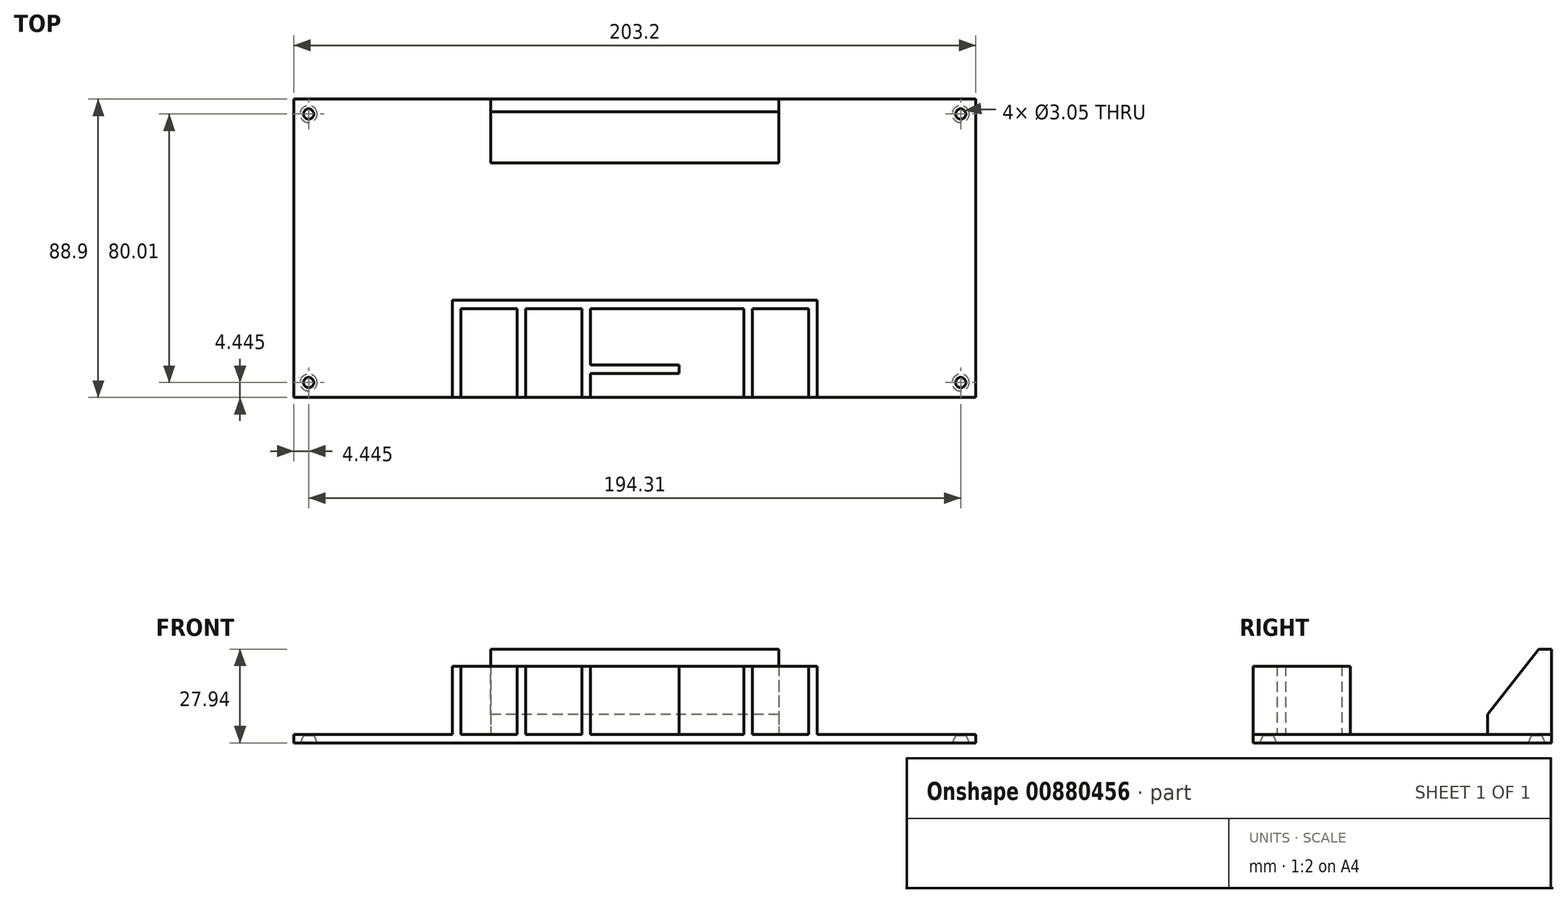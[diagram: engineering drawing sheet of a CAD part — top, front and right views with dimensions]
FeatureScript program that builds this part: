
annotation { "Feature Type Name" : "Feature", "Feature Type Description" : "" }
export const myFeature = defineFeature(function(context is Context, id is Id, definition is map)
    precondition{}
    {
        {
            var Q0;
            Q0=qCreatedBy(makeId("Top.planeOp"),FACE);
            var sketch = newSketch(context, id + "F0", { "sketchPlane" : qUnion([Q0])});
            skLineSegment(sketch, "E0.bottom", {"start": v(101.6, -44.45) * mm, "end": v(-101.6, -44.45) * mm});
            skLineSegment(sketch, "E0.top", {"start": v(101.6, 44.45) * mm, "end": v(-101.6, 44.45) * mm});
            skLineSegment(sketch, "E0.left", {"start": v(101.6, -44.45) * mm, "end": v(101.6, 44.45) * mm});
            skLineSegment(sketch, "E0.right", {"start": v(-101.6, -44.45) * mm, "end": v(-101.6, 44.45) * mm});
            skPoint(sketch, "E0.middle", {"position": v(0, 0) * mm});
            skSolve(sketch);
        }
        {
            var Q0;
            Q0 = qSketchRegion(id + "F0", true);
            extrude(context, id + "F1", {"entities" : qUnion([Q0]), "depth" : 2.54 * mm, "offsetDistance" : 25.4 * mm});
        }
        {
            var Q0;
            Q0=makeQuery(id+"F1.opExtrude","CAP_FACE",FACE,{"disambiguationData":[OSD([sQuery(id+"F0.wireOp",EDGE,"E0.bottom"),sQuery(id+"F0.wireOp",EDGE,"E0.top"),sQuery(id+"F0.wireOp",EDGE,"E0.left"),sQuery(id+"F0.wireOp",EDGE,"E0.right")])],"isStart":false});
            var sketch = newSketch(context, id + "F2", { "sketchPlane" : qUnion([Q0])});
            skLineSegment(sketch, "E1.bottom", {"start": v(-15.75, -44.45) * mm, "end": v(15.75, -44.45) * mm});
            skLineSegment(sketch, "E1.left", {"start": v(-15.75, -44.45) * mm, "end": v(-15.75, -15.5) * mm});
            skLineSegment(sketch, "E1.right", {"start": v(15.75, -44.45) * mm, "end": v(15.75, -15.5) * mm});
            skLineSegment(sketch, "E2.bottom", {"start": v(-32.51, -44.45) * mm, "end": v(-35.05, -44.45) * mm});
            skLineSegment(sketch, "E2.left", {"start": v(-32.51, -44.45) * mm, "end": v(-32.51, -15.5) * mm});
            skLineSegment(sketch, "E2.right", {"start": v(-35.05, -44.45) * mm, "end": v(-35.05, -15.5) * mm});
            skLineSegment(sketch, "E3.bottom", {"start": v(-54.36, -44.45) * mm, "end": v(-51.82, -44.45) * mm});
            skLineSegment(sketch, "E3.left", {"start": v(-54.36, -44.45) * mm, "end": v(-54.36, -15.5) * mm});
            skLineSegment(sketch, "E3.right", {"start": v(-51.82, -44.45) * mm, "end": v(-51.82, -15.5) * mm});
            skLineSegment(sketch, "E4.bottom", {"start": v(32.51, -44.45) * mm, "end": v(35.05, -44.45) * mm});
            skLineSegment(sketch, "E4.left", {"start": v(32.51, -44.45) * mm, "end": v(32.51, -15.5) * mm});
            skLineSegment(sketch, "E4.right", {"start": v(35.05, -44.45) * mm, "end": v(35.05, -15.5) * mm});
            skLineSegment(sketch, "E5.bottom", {"start": v(51.82, -44.45) * mm, "end": v(54.36, -44.45) * mm});
            skLineSegment(sketch, "E5.left", {"start": v(51.82, -44.45) * mm, "end": v(51.82, -15.5) * mm});
            skLineSegment(sketch, "E5.right", {"start": v(54.36, -44.45) * mm, "end": v(54.36, -15.5) * mm});
            skLineSegment(sketch, "E6", {"start": v(-54.36, -15.5) * mm, "end": v(54.36, -15.5) * mm});
            skLineSegment(sketch, "E7", {"start": v(-54.36, -18.03) * mm, "end": v(51.82, -18.03) * mm});
            skLineSegment(sketch, "E8", {"start": v(51.82, -18.03) * mm, "end": v(54.36, -18.03) * mm});
            skLineSegment(sketch, "E9", {"start": v(-13.2, -44.45) * mm, "end": v(-13.2, -15.5) * mm});
            skLineSegment(sketch, "E10", {"start": v(13.2, -44.45) * mm, "end": v(13.2, -15.5) * mm});
            skLineSegment(sketch, "E11", {"start": v(-13.2, -34.8) * mm, "end": v(13.2, -34.8) * mm});
            skLineSegment(sketch, "E12", {"start": v(13.2, -34.8) * mm, "end": v(13.2, -37.34) * mm});
            skLineSegment(sketch, "E13", {"start": v(13.2, -37.34) * mm, "end": v(-13.2, -37.34) * mm});
            skLineSegment(sketch, "E14.bottom", {"start": v(-42.91, 25.4) * mm, "end": v(42.91, 25.4) * mm});
            skLineSegment(sketch, "E14.top", {"start": v(-42.91, 63.5) * mm, "end": v(42.91, 63.5) * mm});
            skLineSegment(sketch, "E14.left", {"start": v(-42.91, 25.4) * mm, "end": v(-42.91, 63.5) * mm});
            skLineSegment(sketch, "E14.right", {"start": v(42.91, 25.4) * mm, "end": v(42.91, 63.5) * mm});
            skPoint(sketch, "E14.middle", {"position": v(0, 44.45) * mm});
            skLineSegment(sketch, "E15", {"start": v(-42.91, 44.45) * mm, "end": v(42.91, 44.45) * mm});
            skSolve(sketch);
        }
        {
            var Q0;
            {var subQ0=sQuery(id+"F2.wireOp",EDGE,"E2.bottom");Q0=makeQuery(id+"F2.imprint","IMPRINT",FACE,{"disambiguationData":[TD([[makeQuery(id+"F2.imprint","IMPRINT",EDGE,{"derivedFrom":subQ0}),-1.0]])]});}
            var Q1;
            {var subQ0=sQuery(id+"F2.wireOp",EDGE,"E3.bottom");Q1=makeQuery(id+"F2.imprint","IMPRINT",FACE,{"disambiguationData":[TD([[makeQuery(id+"F2.imprint","IMPRINT",EDGE,{"derivedFrom":subQ0}),-1.0]])]});}
            var Q2;
            {var subQ0=sQuery(id+"F2.wireOp",EDGE,"E6");var subQ1=sQuery(id+"F2.wireOp",EDGE,"E3.left");var subQ2=makeQuery(id+"F2.imprint","INTERSECT",VERTEX,{"derivedFrom":[subQ1,subQ0]});Q2=makeQuery(id+"F2.imprint","IMPRINT",FACE,{"disambiguationData":[TD([[makeQuery(id+"F2.imprint","IMPRINT",EDGE,{"disambiguationData":[TD([[subQ2,1.0]])],"derivedFrom":subQ1}),-1.0]])]});}
            var Q3;
            {var subQ0=sQuery(id+"F2.wireOp",EDGE,"E4.bottom");Q3=makeQuery(id+"F2.imprint","IMPRINT",FACE,{"disambiguationData":[TD([[makeQuery(id+"F2.imprint","IMPRINT",EDGE,{"derivedFrom":subQ0}),-1.0]])]});}
            var Q4;
            {var subQ0=sQuery(id+"F2.wireOp",EDGE,"E5.bottom");Q4=makeQuery(id+"F2.imprint","IMPRINT",FACE,{"disambiguationData":[TD([[makeQuery(id+"F2.imprint","IMPRINT",EDGE,{"derivedFrom":subQ0}),-1.0]])]});}
            var Q5;
            {var subQ3=sQuery(id+"F2.wireOp",EDGE,"E8");Q5=makeQuery(id+"F2.imprint","IMPRINT",FACE,{"disambiguationData":[TD([[makeQuery(id+"F2.imprint","IMPRINT",EDGE,{"derivedFrom":subQ3}),1.0]])]});}
            var Q6;
            {var subQ0=sQuery(id+"F2.wireOp",EDGE,"E6");var subQ1=sQuery(id+"F2.wireOp",EDGE,"E1.left");var subQ2=makeQuery(id+"F2.imprint","INTERSECT",VERTEX,{"derivedFrom":[subQ1,subQ0]});Q6=makeQuery(id+"F2.imprint","IMPRINT",FACE,{"disambiguationData":[TD([[makeQuery(id+"F2.imprint","IMPRINT",EDGE,{"disambiguationData":[TD([[subQ2,1.0]])],"derivedFrom":subQ1}),1.0]])]});}
            var Q7;
            {var subQ0=sQuery(id+"F2.wireOp",EDGE,"E6");var subQ1=sQuery(id+"F2.wireOp",EDGE,"E1.left");var subQ2=makeQuery(id+"F2.imprint","INTERSECT",VERTEX,{"derivedFrom":[subQ1,subQ0]});Q7=makeQuery(id+"F2.imprint","IMPRINT",FACE,{"disambiguationData":[TD([[makeQuery(id+"F2.imprint","IMPRINT",EDGE,{"disambiguationData":[TD([[subQ2,1.0]])],"derivedFrom":subQ1}),-1.0]])]});}
            var Q8;
            {var subQ0=sQuery(id+"F2.wireOp",EDGE,"E6");var subQ1=sQuery(id+"F2.wireOp",EDGE,"E1.right");var subQ2=makeQuery(id+"F2.imprint","INTERSECT",VERTEX,{"derivedFrom":[subQ1,subQ0]});Q8=makeQuery(id+"F2.imprint","IMPRINT",FACE,{"disambiguationData":[TD([[makeQuery(id+"F2.imprint","IMPRINT",EDGE,{"disambiguationData":[TD([[subQ2,1.0]])],"derivedFrom":subQ1}),-1.0]])]});}
            var Q9;
            {var subQ0=sQuery(id+"F2.wireOp",EDGE,"E6");var subQ1=sQuery(id+"F2.wireOp",EDGE,"E1.right");var subQ2=makeQuery(id+"F2.imprint","INTERSECT",VERTEX,{"derivedFrom":[subQ1,subQ0]});Q9=makeQuery(id+"F2.imprint","IMPRINT",FACE,{"disambiguationData":[TD([[makeQuery(id+"F2.imprint","IMPRINT",EDGE,{"disambiguationData":[TD([[subQ2,1.0]])],"derivedFrom":subQ1}),1.0]])]});}
            var Q10;
            {var subQ0=sQuery(id+"F2.wireOp",EDGE,"E6");var subQ1=sQuery(id+"F2.wireOp",EDGE,"E2.left");var subQ2=makeQuery(id+"F2.imprint","INTERSECT",VERTEX,{"derivedFrom":[subQ1,subQ0]});Q10=makeQuery(id+"F2.imprint","IMPRINT",FACE,{"disambiguationData":[TD([[makeQuery(id+"F2.imprint","IMPRINT",EDGE,{"disambiguationData":[TD([[subQ2,1.0]])],"derivedFrom":subQ1}),1.0]])]});}
            var Q11;
            {var subQ0=sQuery(id+"F2.wireOp",EDGE,"E6");var subQ1=sQuery(id+"F2.wireOp",EDGE,"E2.right");var subQ2=makeQuery(id+"F2.imprint","INTERSECT",VERTEX,{"derivedFrom":[subQ1,subQ0]});Q11=makeQuery(id+"F2.imprint","IMPRINT",FACE,{"disambiguationData":[TD([[makeQuery(id+"F2.imprint","IMPRINT",EDGE,{"disambiguationData":[TD([[subQ2,1.0]])],"derivedFrom":subQ1}),1.0]])]});}
            var Q12;
            {var subQ0=sQuery(id+"F2.wireOp",EDGE,"E6");var subQ1=sQuery(id+"F2.wireOp",EDGE,"E4.left");var subQ2=makeQuery(id+"F2.imprint","INTERSECT",VERTEX,{"derivedFrom":[subQ1,subQ0]});Q12=makeQuery(id+"F2.imprint","IMPRINT",FACE,{"disambiguationData":[TD([[makeQuery(id+"F2.imprint","IMPRINT",EDGE,{"disambiguationData":[TD([[subQ2,1.0]])],"derivedFrom":subQ1}),-1.0]])]});}
            var Q13;
            {var subQ0=sQuery(id+"F2.wireOp",EDGE,"E6");var subQ1=sQuery(id+"F2.wireOp",EDGE,"E4.right");var subQ2=makeQuery(id+"F2.imprint","INTERSECT",VERTEX,{"derivedFrom":[subQ1,subQ0]});Q13=makeQuery(id+"F2.imprint","IMPRINT",FACE,{"disambiguationData":[TD([[makeQuery(id+"F2.imprint","IMPRINT",EDGE,{"disambiguationData":[TD([[subQ2,1.0]])],"derivedFrom":subQ1}),-1.0]])]});}
            var Q14;
            {var subQ0=sQuery(id+"F2.wireOp",EDGE,"E9");var subQ1=sQuery(id+"F2.wireOp",EDGE,"E6");var subQ2=makeQuery(id+"F2.imprint","INTERSECT",VERTEX,{"derivedFrom":[subQ1,subQ0]});Q14=makeQuery(id+"F2.imprint","IMPRINT",FACE,{"disambiguationData":[TD([[makeQuery(id+"F2.imprint","IMPRINT",EDGE,{"disambiguationData":[TD([[subQ2,-1.0]])],"derivedFrom":subQ1}),-1.0]])]});}
            var Q15;
            {var subQ3=sQuery(id+"F2.wireOp",EDGE,"E12");Q15=makeQuery(id+"F2.imprint","IMPRINT",FACE,{"disambiguationData":[TD([[makeQuery(id+"F2.imprint","IMPRINT",EDGE,{"derivedFrom":subQ3}),1.0]])]});}
            var Q16;
            {var subQ4=sQuery(id+"F2.wireOp",EDGE,"E1.left");var subQ6=sQuery(id+"F2.wireOp",EDGE,"E7");var subQ7=makeQuery(id+"F2.imprint","INTERSECT",VERTEX,{"derivedFrom":[subQ4,subQ6]});Q16=makeQuery(id+"F2.imprint","IMPRINT",FACE,{"disambiguationData":[TD([[makeQuery(id+"F2.imprint","IMPRINT",EDGE,{"disambiguationData":[TD([[subQ7,-1.0]])],"derivedFrom":subQ6}),-1.0]])]});}
            var Q17;
            {var subQ0=sQuery(id+"F2.wireOp",EDGE,"E11");Q17=makeQuery(id+"F2.imprint","IMPRINT",FACE,{"disambiguationData":[TD([[makeQuery(id+"F2.imprint","IMPRINT",EDGE,{"derivedFrom":subQ0}),-1.0]])]});}
            extrude(context, id + "F3", {"entities" : qUnion([Q0, Q1, Q2, Q3, Q4, Q5, Q6, Q7, Q8, Q9, Q10, Q11, Q12, Q13, Q14, Q15, Q16, Q17]), "operationType" : NewBodyOperationType.ADD, "depth" : 20.32 * mm, "offsetDistance" : 25.4 * mm});
        }
        {
            var Q0;
            Q0=makeQuery(id+"F1.opExtrude","CAP_FACE",FACE,{"disambiguationData":[OSD([sQuery(id+"F0.wireOp",EDGE,"E0.bottom"),sQuery(id+"F0.wireOp",EDGE,"E0.top"),sQuery(id+"F0.wireOp",EDGE,"E0.left"),sQuery(id+"F0.wireOp",EDGE,"E0.right")])],"isStart":true});
            var sketch = newSketch(context, id + "F4", { "sketchPlane" : qUnion([Q0])});
            skPoint(sketch, "E16", {"position": v(97.15, -40) * mm});
            skPoint(sketch, "E17", {"position": v(-97.16, -40) * mm});
            skPoint(sketch, "E18", {"position": v(-97.16, 40) * mm});
            skPoint(sketch, "E19", {"position": v(97.15, 40) * mm});
            skSolve(sketch);
        }
        {
            var Q0;
            Q0=sQuery(id+"F4.wireOp",VERTEX,"E16");
            var Q1;
            Q1=sQuery(id+"F4.wireOp",VERTEX,"E19");
            var Q2;
            Q2=sQuery(id+"F4.wireOp",VERTEX,"E18");
            var Q3;
            Q3=sQuery(id+"F4.wireOp",VERTEX,"E17");
            var Q4;
            Q4=makeQuery(id+"F1.opExtrude","SWEPT_BODY",BODY,{"disambiguationData":[OSD([sQuery(id+"F0.wireOp",EDGE,"E0.bottom"),sQuery(id+"F0.wireOp",EDGE,"E0.top"),sQuery(id+"F0.wireOp",EDGE,"E0.left"),sQuery(id+"F0.wireOp",EDGE,"E0.right")])]});
            hole(context, id + "F5", {"style" : HoleStyle.C_SINK, "endStyle" : HoleEndStyle.THROUGH, "holeDiameter" : 3.05 * mm, "cSinkDiameter" : 5.08 * mm, "cSinkAngle" : 49 * degree, "majorDiameter" : 6.35 * mm, "isTappedThrough" : true, "tappedDepth" : 12.7 * mm, "tapClearance" : 3, "locations" : qUnion([Q0, Q1, Q2, Q3]), "scope" : qUnion([Q4])});
        }
        {
            var Q0;
            {var subQ0=sQuery(id+"F2.wireOp",EDGE,"E14.bottom");Q0=makeQuery(id+"F2.imprint","IMPRINT",FACE,{"disambiguationData":[TD([[makeQuery(id+"F2.imprint","IMPRINT",EDGE,{"derivedFrom":subQ0}),1.0]])]});}
            extrude(context, id + "F6", {"entities" : qUnion([Q0]), "operationType" : NewBodyOperationType.ADD, "depth" : 25.4 * mm, "offsetDistance" : 25.4 * mm});
        }
        {
            var Q0;
            Q0=makeQuery(id+"F6.opExtrude","CAP_EDGE",EDGE,{"disambiguationData":[OSD([sQuery(id+"F2.wireOp",EDGE,"E14.bottom")])],"isStart":false});
            chamfer(context, id + "F7", {"entities" : qUnion([Q0]), "chamferType" : ChamferType.OFFSET_ANGLE, "width" : 15.24 * mm, "oppositeDirection" : false, "angle" : 52 * degree, "tangentPropagation" : true});
        }
    });
